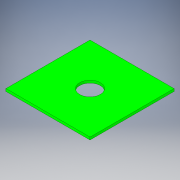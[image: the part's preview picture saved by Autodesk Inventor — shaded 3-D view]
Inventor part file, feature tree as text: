
AUTODESK INVENTOR PART (.ipt)
format: ipt  version: 2019 (Build 230136000, 136)  size: 108,544 bytes
history: native  units: mm
features: extrude x1, sketch x1
ambient origin geometry x8: Origin, YZ Plane, XZ Plane, XY Plane, X Axis, Y Axis, Z Axis, Center Point
bodies: Solid1 (feature_tree)
feature tree (2):
  extrude  "Extrusion1"  Depth=106.36mm
  sketch  "Sketch1"  dims[d0=106.36mm d1=106.36mm d2=26.0mm d3=3.18mm d4=0.0mm]
